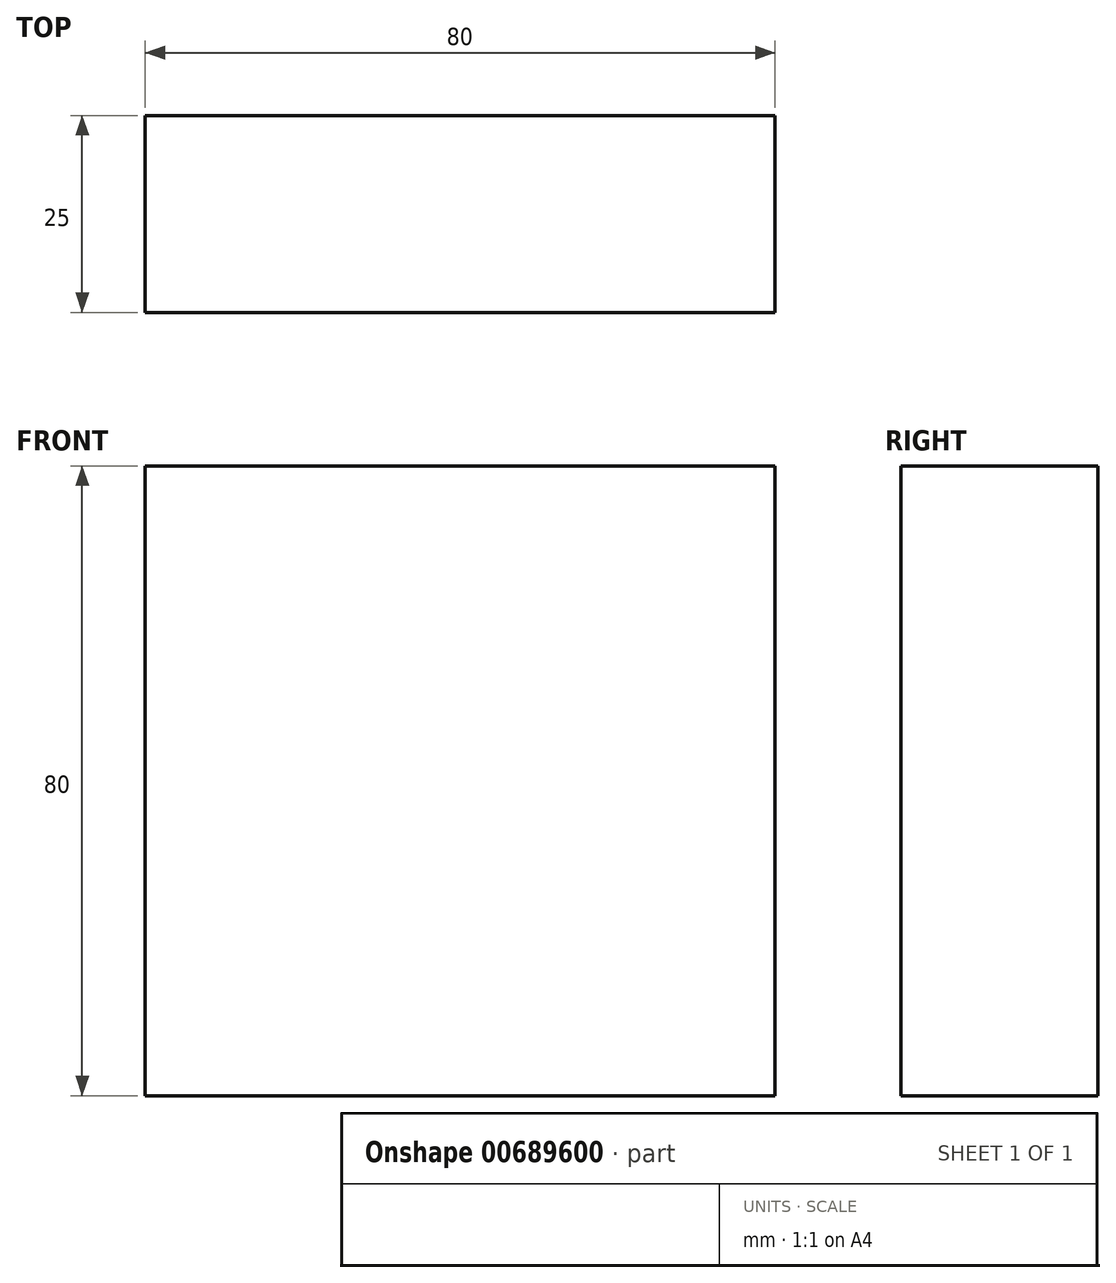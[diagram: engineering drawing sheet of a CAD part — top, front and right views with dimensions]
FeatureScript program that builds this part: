
annotation { "Feature Type Name" : "Feature", "Feature Type Description" : "" }
export const myFeature = defineFeature(function(context is Context, id is Id, definition is map)
    precondition{}
    {
        {
            var Q0;
            Q0=qCreatedBy(makeId("Front.planeOp"),FACE);
            var sketch = newSketch(context, id + "F0", { "sketchPlane" : qUnion([Q0])});
            skLineSegment(sketch, "E0.bottom", {"start": v(0, 0) * mm, "end": v(-80, 0) * mm});
            skLineSegment(sketch, "E0.top", {"start": v(0, 80) * mm, "end": v(-80, 80) * mm});
            skLineSegment(sketch, "E0.left", {"start": v(0, 0) * mm, "end": v(0, 80) * mm});
            skLineSegment(sketch, "E0.right", {"start": v(-80, 0) * mm, "end": v(-80, 80) * mm});
            skSolve(sketch);
        }
        {
            var Q0;
            Q0=makeQuery(id+"F0.imprint","IMPRINT",FACE,{"disambiguationData":[TD([[makeQuery(id+"F0.imprint","IMPRINT",EDGE,{"derivedFrom":sQuery(id+"F0.wireOp",EDGE,"E0.bottom")}),-1.0]])]});
            extrude(context, id + "F1", {"entities" : qUnion([Q0]), "depth" : 25 * mm, "offsetDistance" : 25 * mm});
        }
    });
